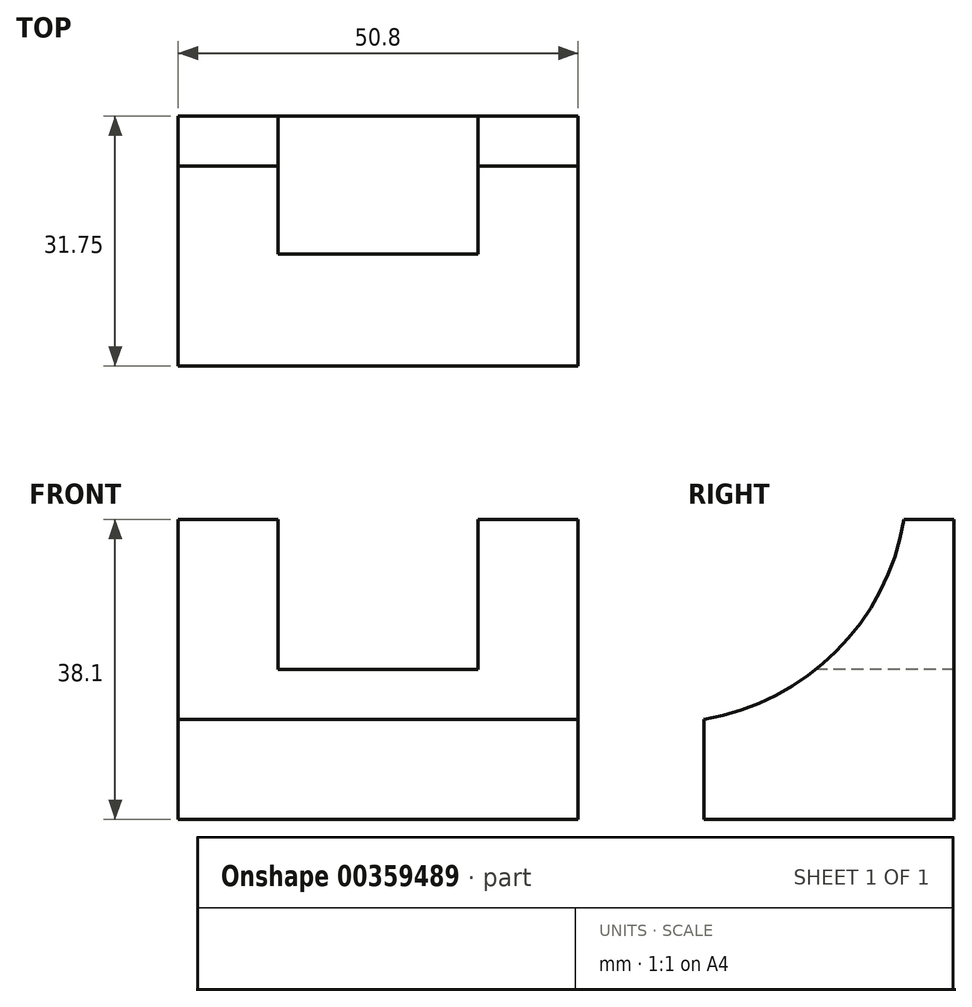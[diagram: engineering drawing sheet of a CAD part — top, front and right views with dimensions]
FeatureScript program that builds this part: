
annotation { "Feature Type Name" : "Feature", "Feature Type Description" : "" }
export const myFeature = defineFeature(function(context is Context, id is Id, definition is map)
    precondition{}
    {
        {
            var Q0;
            Q0=qCreatedBy(makeId("Front.planeOp"),FACE);
            var sketch = newSketch(context, id + "F0", { "sketchPlane" : qUnion([Q0])});
            skLineSegment(sketch, "E0", {"start": v(0, 38.1) * mm, "end": v(0, 0) * mm});
            skLineSegment(sketch, "E1", {"start": v(0, 0) * mm, "end": v(50.8, 0) * mm});
            skLineSegment(sketch, "E2", {"start": v(50.8, 0) * mm, "end": v(50.8, 38.1) * mm});
            skLineSegment(sketch, "E3", {"start": v(50.8, 38.1) * mm, "end": v(0, 38.1) * mm});
            skSolve(sketch);
        }
        {
            var Q0;
            Q0 = qSketchRegion(id + "F0", true);
            extrude(context, id + "F1", {"entities" : qUnion([Q0]), "oppositeDirection" : true, "depth" : 31.75 * mm});
        }
        {
            var Q0;
            Q0=makeQuery(id+"F1.opExtrude","SWEPT_FACE",FACE,{"disambiguationData":[OSD([sQuery(id+"F0.wireOp",EDGE,"E3")])]});
            var sketch = newSketch(context, id + "F2", { "sketchPlane" : qUnion([Q0])});
            skLineSegment(sketch, "E4", {"start": v(12.7, 31.75) * mm, "end": v(12.7, 12.7) * mm});
            skLineSegment(sketch, "E5", {"start": v(12.7, 12.7) * mm, "end": v(38.1, 12.7) * mm});
            skLineSegment(sketch, "E6", {"start": v(38.1, 12.7) * mm, "end": v(38.1, 31.75) * mm});
            skLineSegment(sketch, "E7", {"start": v(38.1, 31.75) * mm, "end": v(12.7, 31.75) * mm});
            skSolve(sketch);
        }
        {
            var Q0;
            Q0 = qSketchRegion(id + "F2", true);
            extrude(context, id + "F3", {"entities" : qUnion([Q0]), "operationType" : NewBodyOperationType.REMOVE, "oppositeDirection" : true, "depth" : 19.05 * mm});
        }
        {
            var Q0;
            Q0=makeQuery(id+"F1.opExtrude","SWEPT_FACE",FACE,{"disambiguationData":[OSD([sQuery(id+"F0.wireOp",EDGE,"E2")])]});
            var sketch = newSketch(context, id + "F4", { "sketchPlane" : qUnion([Q0])});
            skArc(sketch, "E8", {"start": v(0, 12.7) * mm, "mid": v(16.76, 21.34) * mm, "end": v(25.4, 38.1) * mm});
            skLineSegment(sketch, "E9", {"start": v(0, 12.7) * mm, "end": v(0, 38.1) * mm});
            skLineSegment(sketch, "E10", {"start": v(0, 38.1) * mm, "end": v(25.4, 38.1) * mm});
            skSolve(sketch);
        }
        {
            var Q0;
            Q0 = qSketchRegion(id + "F4", true);
            extrude(context, id + "F5", {"entities" : qUnion([Q0]), "operationType" : NewBodyOperationType.REMOVE, "oppositeDirection" : true, "depth" : 50.8 * mm});
        }
    });
